# Revit family: Maia FT
name_source: partatom
category: Осветительные приборы
revit_build: Autodesk Revit 2016 (Build: 20150220_1215(x64)
units: mm (PartAtom-declared; Revit-internal decimal feet)

## family parameters
Всегда вертикально = Да
Заголовок OmniClass = Lighting
Источник света = Да
На основе рабочей плоскости = Да
Номер OmniClass = 23.80.70.00
Общий = Нет
При загрузке вырезать с полостями = Нет
Размер круглого соединителя = Использовать диаметр
Тип детали = Нормальный
Точка расчета площади = Нет

## types (4) — shared parameters
A = 150 мм
A1 = 140 мм
ADSK_Единица измерения = Шт.
ADSK_Завод-изготовитель = ООО МГК Световые технологии
ADSK_Количество фаз = 1
ADSK_Количество фаз числовое = 1
ADSK_Наименование = Торшер и настольная лампа. Рассеиватель из выдувного трехслойного опалового стекла, выдуваемого вручную. Металлические части окрашены в белый матовый цвет - WH
ADSK_Напряжение = 230 В
ADSK_Номинальная мощность = 0 кВ·А
ADSK_Полная мощность = 0 кВт
IP Class = IP20
URL = http://www.ltcompany.com
Блок аварийного питания = Нет
Видимая форма излучения при визуализации = Нет
Группа модели = Светильники
Изготовитель = ООО МГК Световые технологии
Излучение по длине прямоугольника = 150 мм
Излучение по ширине прямоугольника = 150 мм
Класс Защиты = II
Климатическая зона = УХЛ4
Код по классификатору = D5020200
Корпус = Белый металл
Область использования = Гостиницы, Индивидуальные дома, Культурно-развлекательные, Магазины/Бутики, Объекты бытового обслуживания, Объекты общественного питания, Офисы, ТРЦ
Описание = Торшер и настольная лампа. Рассеиватель из выдувного трехслойного опалового стекла, выдуваемого вручную. Металлические части окрашены в белый матовый цвет - WH
Плафон = Плафон полупрозрачный
Полная установленная мощность = 0 кВт
Разработчик = ООО ПРОРУБИМ
Разработчик (телефон) = +7 (495) 649-85-43
Светофильтр = 16777215
Смещение цветовой температуры при затухании лампы = <Нет>
Тип ПРА = ЭПРА
Тип продукции = Светильник
Угол наклона = -90.00°
Файл фотометрической сетки = MAIA.ies
zero-valued in all types: Отметка по умолчанию

## per-type parameters (varying)
| type | ADSK_Код изделия | ADSK_Коэффициент мощности | ADSK_Масса | ADSK_Размер_Высота | ADSK_Ток | ADSK_Энергоэффективность | B | D | Тип ИС |
| MAIA T 460 WH 100 | 1535000140 | 0.98 | 4.2 | 460 мм | 0 А | 100 лм/Вт | 300 мм | 160 мм | КЛЛ |
| MAIA F 1750 WH 100 | 1535000070 | 0.98 | 4.8 | 1750 мм | 1 А | 100 лм/Вт | 300 мм | 260 мм | КЛЛ |
| MAIA F 1850 WH 100 | 1535000100 | 1 | 11 | 1850 мм | 1 А | 150 лм/Вт | 500 мм | 260 мм | ЛН |
| MAIA T 700 WH 150 | 1535000060 | 1 | 4.8 | 700 мм | 1 А | 150 лм/Вт | 500 мм | 160 мм | ЛН |
